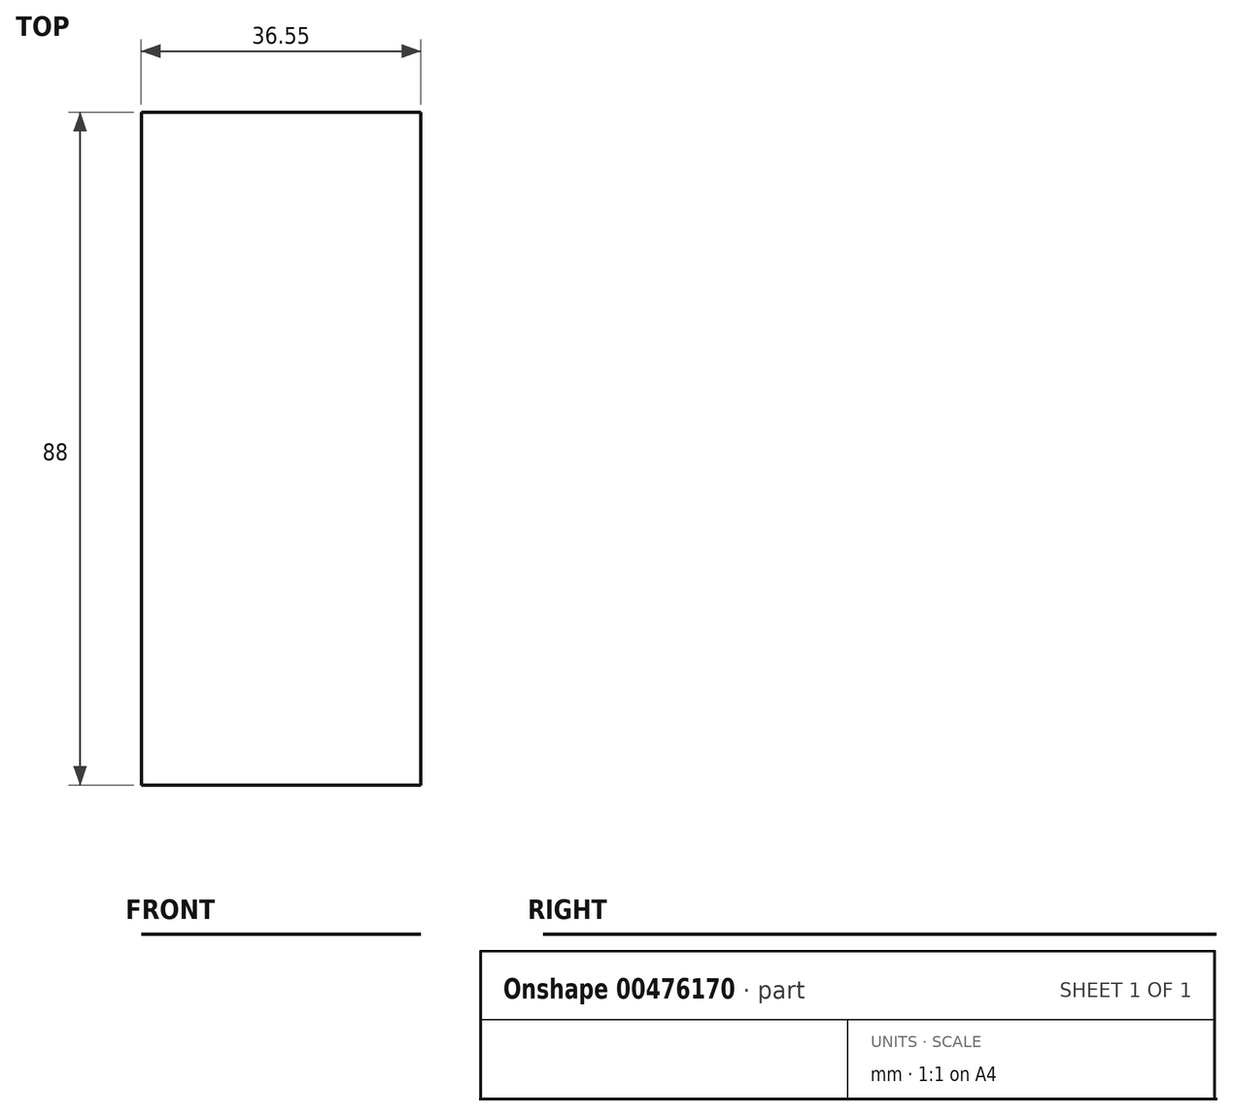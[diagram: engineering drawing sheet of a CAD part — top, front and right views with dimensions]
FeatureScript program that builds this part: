
annotation { "Feature Type Name" : "Feature", "Feature Type Description" : "" }
export const myFeature = defineFeature(function(context is Context, id is Id, definition is map)
    precondition{}
    {
        {
            var Q0;
            Q0=qCreatedBy(makeId("Front.planeOp"),FACE);
            var sketch = newSketch(context, id + "F0", { "sketchPlane" : qUnion([Q0])});
            skLineSegment(sketch, "E0", {"start": v(-131.14, 12.01) * mm, "end": v(-131.14, 51.7) * mm});
            skLineSegment(sketch, "E1", {"start": v(-119.68, 51.43) * mm, "end": v(-83.13, 51.43) * mm});
            skSolve(sketch);
        }
        {
            var Q0;
            Q0=sQuery(id+"F0.wireOp",EDGE,"E1");
            extrude(context, id + "F1", {"bodyType" : ToolBodyType.SURFACE, "surfaceEntities" : qUnion([Q0]), "depth" : 88 * mm});
        }
    });
